FCSTD DOCUMENT  (FreeCAD 1.0RUnknown)
Label: lever-plate
License: All rights reserved
LicenseURL: https://en.wikipedia.org/wiki/All_rights_reserved
objects: Image::ImagePlane×1, Sketcher::SketchObject×1, PartDesign::Body×1, Spreadsheet::Sheet×1
note: 3 computed .brp shape members not serialized (recipe doc carries the construction recipe); baked Part::Feature solids carry a one-line shape summary decoded from their .brp

FEATURE [Image::ImagePlane] lever_plate  label="lever-plate"
  Placement = pos=(-60.62,0,41.98) rot=(0.998783,0.034878,0.034878;4.71117rad)
  XSize = 187.405
  YSize = 278.314
FEATURE [Sketcher::SketchObject] Sketch
  ArcFitTolerance = 1e-06
  AttachmentSupport = -> [XZ_Plane]
  FullyConstrained = false
  MakeInternals = false
  MapMode = 5
  Placement = pos=(0,0,0) rot=(1,0,0;1.5708rad)
  expr: Constraints[36] = <<Spreadsheet>>.C2
  expr: Constraints[37] = <<Spreadsheet>>.C3
  expr: Constraints[44] = <<Spreadsheet>>.C4
  expr: Constraints[51] = <<Spreadsheet>>.C5
  expr: Constraints[60] = <<Spreadsheet>>.C7
  sketch-geometry (32):
    g0: LineSegment StartX=-30.78 StartY=98.51 StartZ=0 EndX=-30.78 EndY=78.59 EndZ=0
    g1: LineSegment StartX=-30.78 StartY=78.59 StartZ=0 EndX=-26.96 EndY=78.59 EndZ=0
    g2: LineSegment StartX=-26.96 StartY=78.59 StartZ=0 EndX=-26.96 EndY=85.295 EndZ=0
    g3: LineSegment StartX=-26.96 StartY=98.51 StartZ=0 EndX=-30.78 EndY=98.51 EndZ=0
    g4: LineSegment StartX=-26.96 StartY=85.295 StartZ=0 EndX=-25.18 EndY=85.295 EndZ=0
    g5: LineSegment StartX=-25.18 StartY=85.295 StartZ=0 EndX=-25.18 EndY=91.805 EndZ=0
    g6: LineSegment StartX=-25.18 StartY=91.805 StartZ=0 EndX=-26.96 EndY=91.805 EndZ=0
    g7: LineSegment StartX=-26.96 StartY=91.805 StartZ=0 EndX=-26.96 EndY=98.51 EndZ=0
    g8: LineSegment StartX=13.32 StartY=78.59 StartZ=0 EndX=13.32 EndY=98.51 EndZ=0
    g9: LineSegment StartX=13.32 StartY=78.59 StartZ=0 EndX=15.15 EndY=78.59 EndZ=0
    g10: LineSegment [constr] StartX=-26.96 StartY=98.51 StartZ=0 EndX=13.32 EndY=98.51 EndZ=0
    g11: LineSegment [constr] StartX=-26.96 StartY=78.59 StartZ=0 EndX=13.32 EndY=78.59 EndZ=0
    g12: LineSegment StartX=13.32 StartY=98.51 StartZ=0 EndX=16.13 EndY=98.51 EndZ=0
    g13: Circle CenterX=0 CenterY=0 CenterZ=0 NormalX=0 NormalY=0 NormalZ=1 AngleXU=0 Radius=2.355
    g14: Circle CenterX=-131.1 CenterY=62.07 CenterZ=0 NormalX=0 NormalY=0 NormalZ=1 AngleXU=0 Radius=2.45
    g15: ArcOfCircle CenterX=-131.1 CenterY=62.07 CenterZ=0 NormalX=0 NormalY=0 NormalZ=1 AngleXU=0 Radius=12.23 StartAngle=0.841275 EndAngle=5.40235
    g16: LineSegment StartX=-69.2092 StartY=117.073 StartZ=0 EndX=-65.4739 EndY=110.754 EndZ=0
    g17: LineSegment [constr] StartX=-65.4739 StartY=110.754 StartZ=0 EndX=0 EndY=0 EndZ=0
    g18: ArcOfCircle CenterX=0 CenterY=0 CenterZ=0 NormalX=0 NormalY=0 NormalZ=1 AngleXU=0 Radius=136 StartAngle=1.69873 EndAngle=2.10469
    g19: ArcOfCircle CenterX=0 CenterY=0 CenterZ=0 NormalX=0 NormalY=0 NormalZ=1 AngleXU=0 Radius=128.66 StartAngle=2.10469 EndAngle=2.51066
    g20: LineSegment StartX=15.6728 StartY=138.063 StartZ=0 EndX=18.6129 EndY=129.37 EndZ=0
    g21: LineSegment StartX=-17.3514 StartY=134.889 StartZ=0 EndX=15.6728 EndY=138.063 EndZ=0
    g22: LineSegment StartX=18.6129 StartY=129.37 StartZ=0 EndX=16.13 EndY=112.11 EndZ=0
    g23: LineSegment StartX=16.13 StartY=112.11 StartZ=0 EndX=16.13 EndY=98.51 EndZ=0
    g24: ArcOfCircle CenterX=-118.193 CenterY=92.8618 CenterZ=0 NormalX=0 NormalY=0 NormalZ=1 AngleXU=0 Radius=22.19 StartAngle=4.4964 EndAngle=5.41286
    g25: LineSegment [constr] StartX=-103.89 StartY=75.8967 StartZ=0 EndX=0 EndY=0 EndZ=0
    g26: LineSegment [constr] StartX=-17.3514 StartY=134.889 StartZ=0 EndX=0 EndY=0 EndZ=0
    g27: ArcOfCircle CenterX=-117.926 CenterY=124.3 CenterZ=0 NormalX=0 NormalY=0 NormalZ=1 AngleXU=0 Radius=71.8653 StartAngle=4.63733 EndAngle=5.26155
    g28: ArcOfCircle CenterX=-32.5105 CenterY=-0.992241 CenterZ=0 NormalX=0 NormalY=0 NormalZ=1 AngleXU=0 Radius=79.9379 StartAngle=1.74911 EndAngle=2.21338
    g29: LineSegment StartX=-44.4239 StartY=76.0017 StartZ=0 EndX=-39.7015 EndY=-0.714547 EndZ=0
    g30: LineSegment StartX=-39.7015 StartY=-0.714547 StartZ=0 EndX=-10.1154 EndY=-71.2072 EndZ=0
    g31: ArcOfCircle CenterX=-46.1838 CenterY=75.9922 CenterZ=0 NormalX=0 NormalY=0 NormalZ=1 AngleXU=0 Radius=1.76 StartAngle=0.00537097 EndAngle=1.86184
  constraints (78):
    c: Coincident(g0,g1)
    c: Coincident(g1,g2)
    c: Coincident(g7,g3)
    c: Coincident(g3,g0)
    c: Vertical(g0)
    c: Vertical(g2)
    c: Horizontal(g1)
    c: Horizontal(g3)
    c: Coincident(g4,g5)
    c: Coincident(g5,g6)
    c: Vertical(g5)
    c: Horizontal(g4)
    c: Horizontal(g6)
    c: Distance(g3,g3) = 3.82
    c: DistanceY(g0,g0) = 19.92
    c: Distance(g6,g6) = 1.78
    c: DistanceY(g5,g5) = 6.51
    c: Equal(g2,g7)
    c: Vertical(g7)
    c: Coincident(g2,g4)
    c: Equal(g6,g4)
    c: Coincident(g7,g6)
    c: Vertical(g8)
    c: Coincident(g9,g8)
    c: Horizontal(g9)
    c: Distance(g9,g9) = 1.83
    c: Coincident(g10,g3)
    c: Coincident(g10,g8)
    c: Horizontal(g10)
    c: Coincident(g11,g1)
    c: Coincident(g11,g8)
    c: Horizontal(g11)
    c: Coincident(g12,g8)
    c: Horizontal(g12)
    c: Distance(g12,g12) = 2.81
    c: DistanceX(g11,g11) = 40.28
    c: Diameter(g13) = 4.71
    c: Diameter(g14) = 4.9
    c: DistanceX(g14,g13) = 131.1
    c: DistanceY(g13,g14) = 62.07
    c: Distance(g13,g11) = 78.59
    c: DistanceX(g1,g13) = 26.96
    c: Coincident(g13,g-1)
    c: Coincident(g15,g14)
    c: Diameter(g15) = 24.46
    c: Coincident(g17,g13)
    c: Coincident(g16,g17)
    c: Coincident(g18,g13)
    c: Coincident(g18,g16)
    c: Coincident(g19,g13)
    c: Coincident(g19,g16)
    c: Distance(g16,g16) = 7.34
    c: Distance(g16,g13) = 136  '<<Spreadsheet>>.C6'
    c: Coincident(g20,g22)
    c: Coincident(g21,g18)
    c: Coincident(g21,g20)
    c: Parallel(g16,g17)
    c: Coincident(g23,g22)
    c: Coincident(g23,g12)
    c: Vertical(g23)
    c: Angle(g-2,g17) = 0.533896
    c: Distance(g23,g23) = 13.6
    c: Coincident(g24,g15)
    c: Coincident(g24,g19)
    c: Radius(g24) = 22.19
    c: Coincident(g25,g19)
    c: Angle(g17,g25) = 0.405964
    c: Coincident(g13,g25)
    c: Coincident(g26,g18)
    c: Coincident(g26,g13)
    c: Angle(g26,g17) = 0.405964
    c: Coincident(g27,g15)
    c: Coincident(g28,g27)
    c: DistanceY(g15,g15) = 18.55
    c: Coincident(g30,g29)
    c: Coincident(g31,g28)
    c: Coincident(g31,g29)
    c: Radius(g31) = 1.76
FEATURE [PartDesign::Body] Body
  AllowCompound = false
  Group = -> [Sketch]
  Origin = -> Origin
FEATURE [Spreadsheet::Sheet] Spreadsheet
  cells = B1='Default; C1='Value; A2='Pivot Hole Size; C2==4.71 mm; A3='Handle Knob Hole Size; C3==4.9 mm; A4='Handle Knob Diameter; C4==24.46 mm; A5='Stop Height; C5==7.34 mm; A6='Swing Radius; C6==136 mm; A7='Swing Travel; C7=30.59
